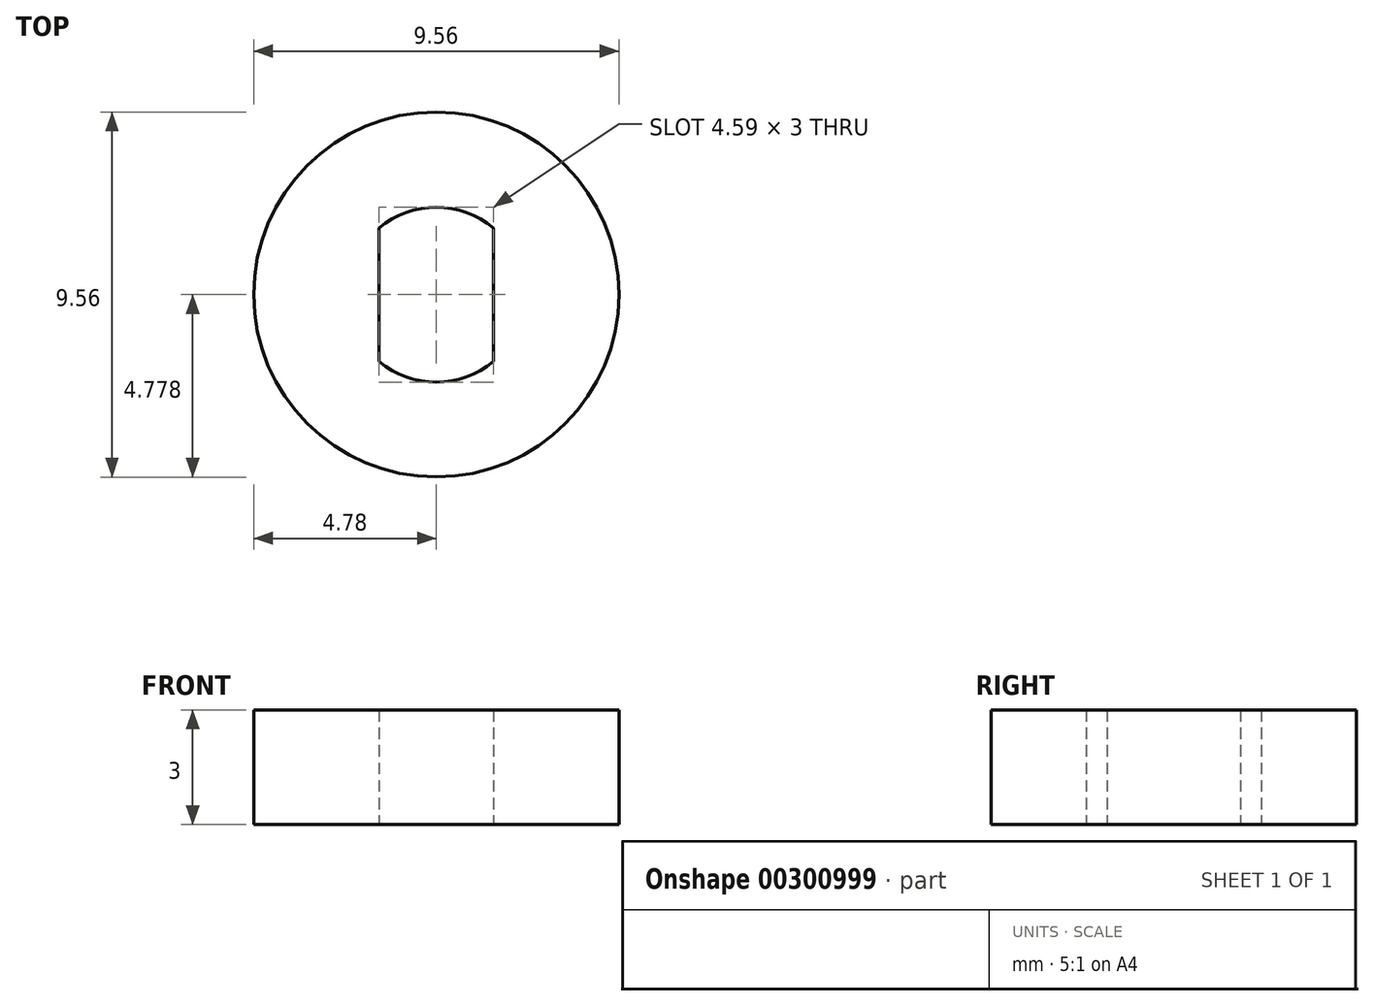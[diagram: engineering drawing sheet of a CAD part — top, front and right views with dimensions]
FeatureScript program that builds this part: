
annotation { "Feature Type Name" : "Feature", "Feature Type Description" : "" }
export const myFeature = defineFeature(function(context is Context, id is Id, definition is map)
    precondition{}
    {
        {
            var Q0;
            Q0=qCreatedBy(makeId("Top.planeOp"),FACE);
            var sketch = newSketch(context, id + "F0", { "sketchPlane" : qUnion([Q0])});
            skLineSegment(sketch, "E0", {"start": v(-1.5, -0.15) * mm, "end": v(-1.5, -3.65) * mm});
            skLineSegment(sketch, "E1.MirrorCS", {"start": v(1.5, -0.15) * mm, "end": v(1.5, -3.65) * mm});
            skArc(sketch, "E2", {"start": v(1.5, -0.15) * mm, "mid": v(0, 0.4) * mm, "end": v(-1.5, -0.15) * mm});
            skArc(sketch, "E3", {"start": v(-1.5, -3.65) * mm, "mid": v(0, -4.2) * mm, "end": v(1.5, -3.65) * mm});
            skCircle(sketch, "E4", {"center": v(0, -1.9) * mm, "radius": 4.78 * mm});
            skSolve(sketch);
        }
        {
            var Q0;
            Q0=makeQuery(id+"F0.imprint","IMPRINT",FACE,{"disambiguationData":[TD([[makeQuery(id+"F0.imprint","IMPRINT",EDGE,{"derivedFrom":sQuery(id+"F0.wireOp",EDGE,"E0")}),-1.0]])]});
            extrude(context, id + "F1", {"entities" : qUnion([Q0]), "depth" : 3 * mm, "offsetDistance" : 25 * mm});
        }
    });
